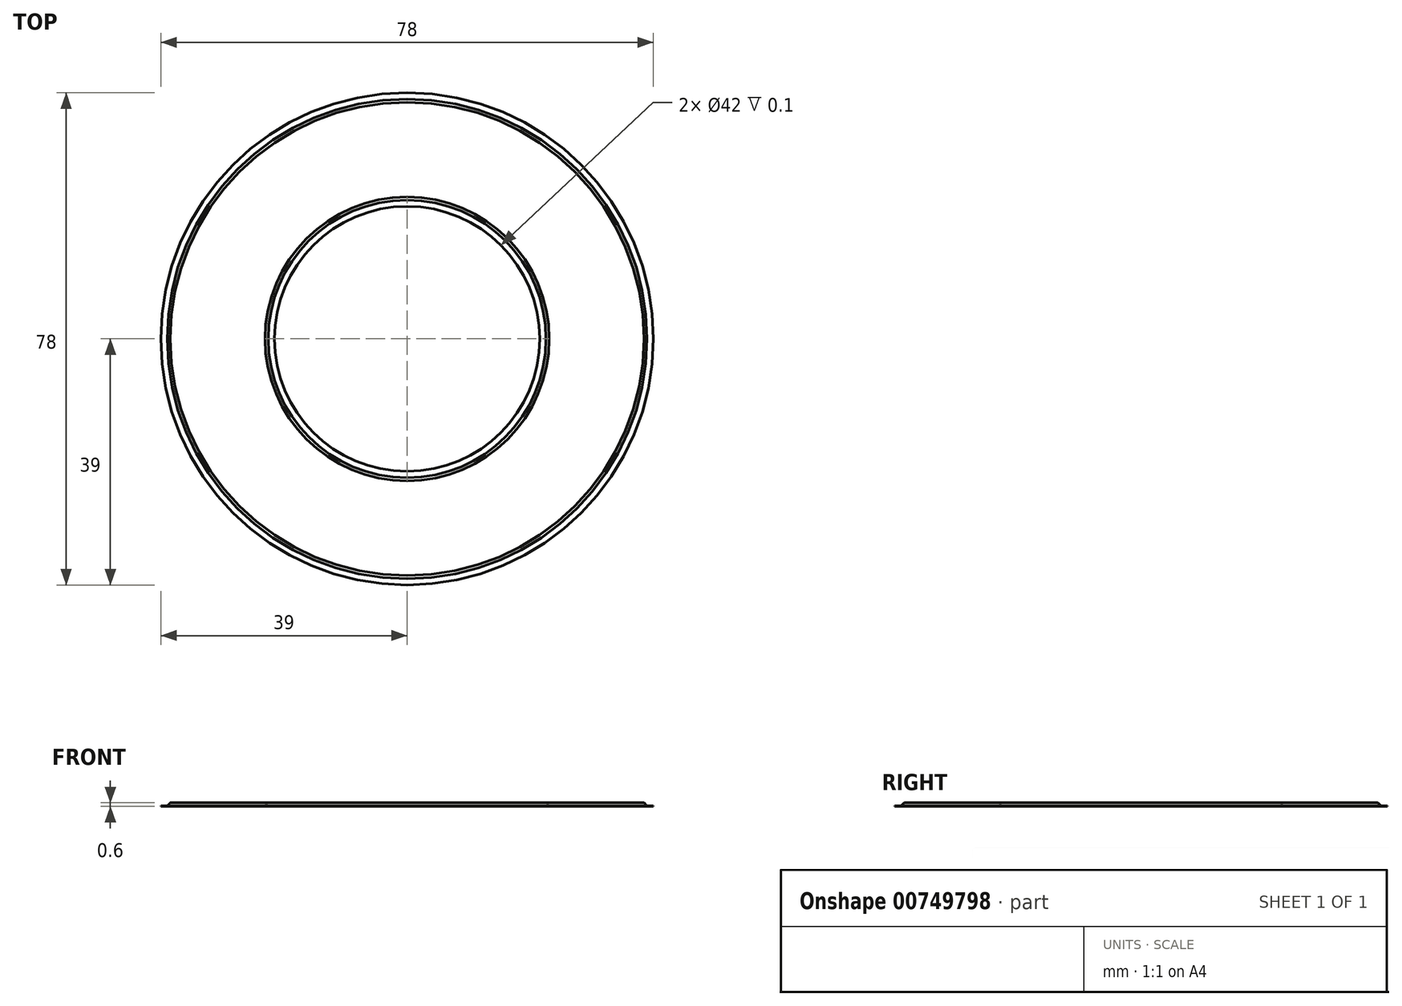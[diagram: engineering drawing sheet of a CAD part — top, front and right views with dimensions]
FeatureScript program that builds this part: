
annotation { "Feature Type Name" : "Feature", "Feature Type Description" : "" }
export const myFeature = defineFeature(function(context is Context, id is Id, definition is map)
    precondition{}
    {
        {
            var Q0;
            Q0=qCreatedBy(makeId("Front.planeOp"),FACE);
            var sketch = newSketch(context, id + "F0", { "sketchPlane" : qUnion([Q0])});
            skPoint(sketch, "E0", {"position": v(21, 0) * mm});
            skPoint(sketch, "E1", {"position": v(21, 0.1) * mm});
            skLineSegment(sketch, "E2", {"start": v(21, 0.1) * mm, "end": v(21, 0) * mm});
            skLineSegment(sketch, "E3", {"start": v(0, 0) * mm, "end": v(0, 5.6) * mm});
            skLineSegment(sketch, "E4", {"start": v(21, 0) * mm, "end": v(22, 0) * mm});
            skLineSegment(sketch, "E5", {"start": v(22, 0) * mm, "end": v(22.5, 0.5) * mm});
            skLineSegment(sketch, "E6", {"start": v(22.5, 0.5) * mm, "end": v(37.5, 0.5) * mm});
            skLineSegment(sketch, "E7", {"start": v(37.5, 0.5) * mm, "end": v(38, 0) * mm});
            skLineSegment(sketch, "E8", {"start": v(38, 0) * mm, "end": v(39, 0) * mm});
            skLineSegment(sketch, "E9", {"start": v(39, 0) * mm, "end": v(39, 0.1) * mm});
            skLineSegment(sketch, "E10", {"start": v(39, 0.1) * mm, "end": v(38, 0.1) * mm});
            skLineSegment(sketch, "E11", {"start": v(38, 0.1) * mm, "end": v(37.5, 0.6) * mm});
            skLineSegment(sketch, "E12", {"start": v(37.5, 0.6) * mm, "end": v(22.5, 0.6) * mm});
            skLineSegment(sketch, "E13", {"start": v(22.5, 0.6) * mm, "end": v(22, 0.1) * mm});
            skLineSegment(sketch, "E14", {"start": v(22, 0.1) * mm, "end": v(21, 0.1) * mm});
            skSolve(sketch);
        }
        {
            var Q0;
            Q0=makeQuery(id+"F0.imprint","IMPRINT",FACE,{"disambiguationData":[TD([[makeQuery(id+"F0.imprint","IMPRINT",EDGE,{"derivedFrom":sQuery(id+"F0.wireOp",EDGE,"E2")}),1.0]])]});
            var Q1;
            Q1=sQuery(id+"F0.wireOp",EDGE,"E3");
            revolve(context, id + "F1", {"surfaceOperationType" : NewSurfaceOperationType.NEW, "entities" : qUnion([Q0]), "axis" : qUnion([Q1]), "revolveType" : RevolveType.FULL});
        }
    });
